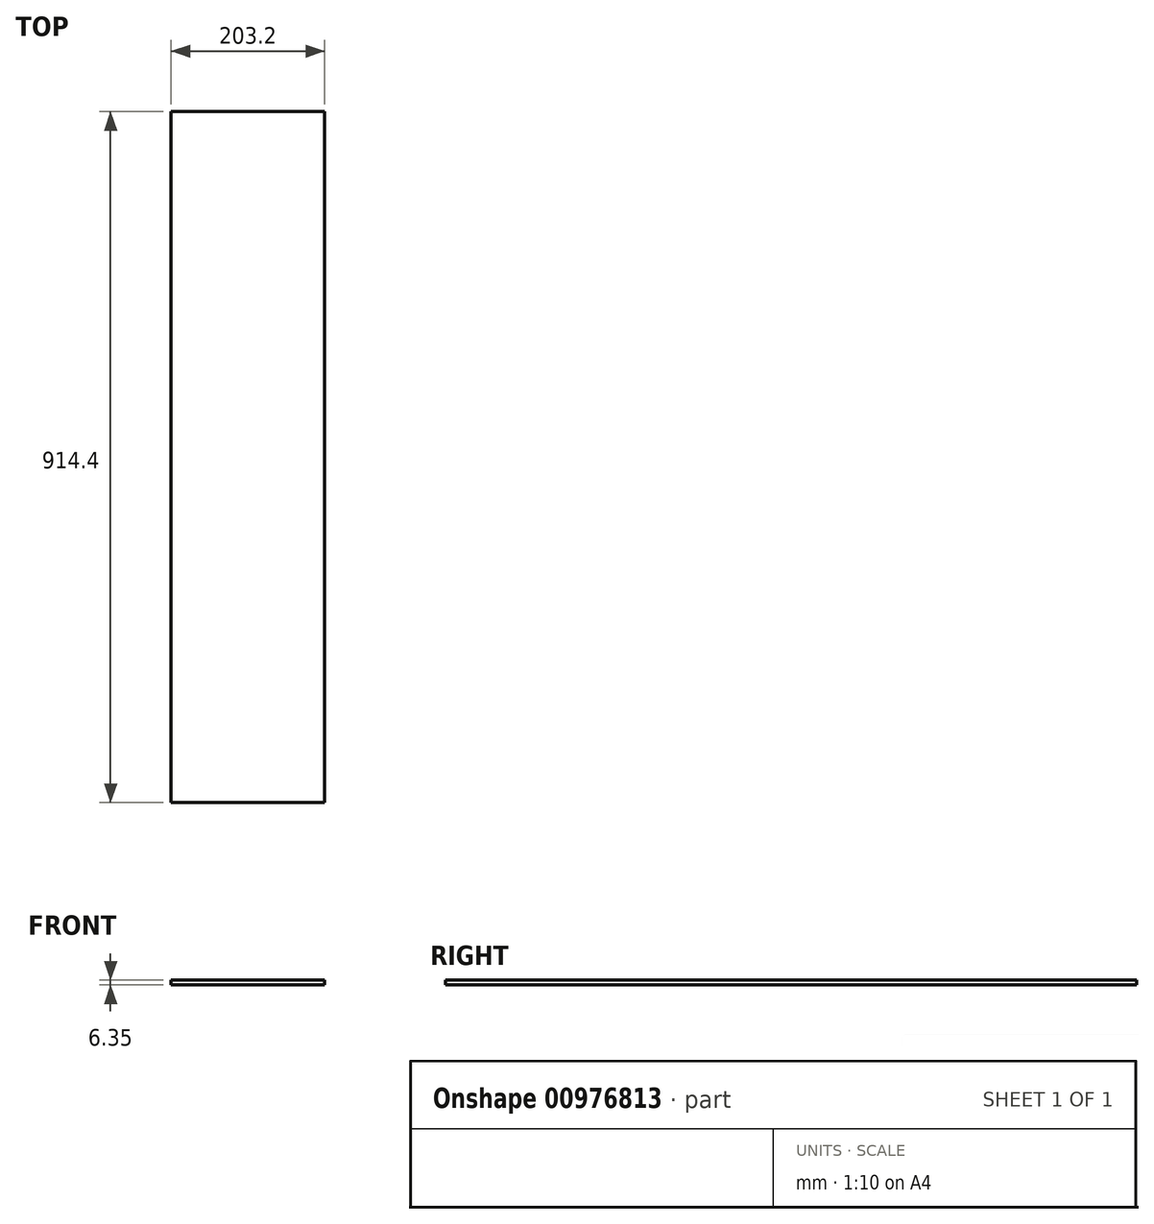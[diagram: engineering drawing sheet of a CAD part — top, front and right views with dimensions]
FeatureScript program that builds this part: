
annotation { "Feature Type Name" : "Feature", "Feature Type Description" : "" }
export const myFeature = defineFeature(function(context is Context, id is Id, definition is map)
    precondition{}
    {
        {
            var Q0;
            Q0=qCreatedBy(makeId("Front.planeOp"),FACE);
            var sketch = newSketch(context, id + "F0", { "sketchPlane" : qUnion([Q0])});
            skLineSegment(sketch, "E0.bottom", {"start": v(0, 0) * mm, "end": v(203.2, 0) * mm});
            skLineSegment(sketch, "E0.top", {"start": v(0, 152.4) * mm, "end": v(203.2, 152.4) * mm});
            skLineSegment(sketch, "E0.left", {"start": v(0, 0) * mm, "end": v(0, 6.35) * mm});
            skLineSegment(sketch, "E0.right", {"start": v(203.2, 0) * mm, "end": v(203.2, 6.35) * mm});
            skLineSegment(sketch, "E1.bottom", {"start": v(203.2, 146.05) * mm, "end": v(104.78, 146.05) * mm});
            skLineSegment(sketch, "E1.top", {"start": v(203.2, 6.35) * mm, "end": v(104.78, 6.35) * mm});
            skLineSegment(sketch, "E1.right", {"start": v(104.78, 146.05) * mm, "end": v(104.78, 15.97) * mm});
            skLineSegment(sketch, "E2.bottom", {"start": v(0, 146.05) * mm, "end": v(98.43, 146.05) * mm});
            skLineSegment(sketch, "E2.top", {"start": v(0, 6.35) * mm, "end": v(98.43, 6.35) * mm});
            skLineSegment(sketch, "E2.right", {"start": v(98.43, 146.05) * mm, "end": v(98.43, 15.97) * mm});
            skLineSegment(sketch, "E3.trimOffspring", {"start": v(203.2, 146.05) * mm, "end": v(203.2, 152.4) * mm});
            skLineSegment(sketch, "E4.trimOffspring", {"start": v(0, 146.05) * mm, "end": v(0, 152.4) * mm});
            skLineSegment(sketch, "E5", {"start": v(98.43, 6.35) * mm, "end": v(104.78, 6.35) * mm});
            skLineSegment(sketch, "E6", {"start": v(98.43, 15.97) * mm, "end": v(104.78, 15.97) * mm});
            skLineSegment(sketch, "E7.bottom", {"start": v(0, 0) * mm, "end": v(6.35, 0) * mm});
            skLineSegment(sketch, "E7.top", {"start": v(0, -31.75) * mm, "end": v(6.35, -31.75) * mm});
            skLineSegment(sketch, "E7.left", {"start": v(0, 0) * mm, "end": v(0, -31.75) * mm});
            skLineSegment(sketch, "E7.right", {"start": v(6.35, 0) * mm, "end": v(6.35, -31.75) * mm});
            skLineSegment(sketch, "E8.bottom", {"start": v(203.2, 0) * mm, "end": v(196.85, 0) * mm});
            skLineSegment(sketch, "E8.top", {"start": v(203.2, -31.75) * mm, "end": v(196.85, -31.75) * mm});
            skLineSegment(sketch, "E8.left", {"start": v(203.2, 0) * mm, "end": v(203.2, -31.75) * mm});
            skLineSegment(sketch, "E8.right", {"start": v(196.85, 0) * mm, "end": v(196.85, -31.75) * mm});
            skSolve(sketch);
        }
        {
            var Q0;
            Q0=makeQuery(id+"F0.imprint","IMPRINT",FACE,{"disambiguationData":[TD([[makeQuery(id+"F0.imprint","IMPRINT",EDGE,{"derivedFrom":sQuery(id+"F0.wireOp",EDGE,"E0.bottom")}),1.0]])]});
            var Q1;
            Q1=makeQuery(id+"F0.imprint","IMPRINT",FACE,{"disambiguationData":[TD([[makeQuery(id+"F0.imprint","IMPRINT",EDGE,{"derivedFrom":sQuery(id+"F0.wireOp",EDGE,"E7.bottom")}),-1.0]])]});
            var Q2;
            Q2=makeQuery(id+"F0.imprint","IMPRINT",FACE,{"disambiguationData":[TD([[makeQuery(id+"F0.imprint","IMPRINT",EDGE,{"derivedFrom":sQuery(id+"F0.wireOp",EDGE,"E8.bottom")}),1.0]])]});
            extrude(context, id + "F1", {"entities" : qUnion([Q0, Q1, Q2]), "oppositeDirection" : true, "depth" : 914.4 * mm, "offsetDistance" : 25.4 * mm});
        }
    });
